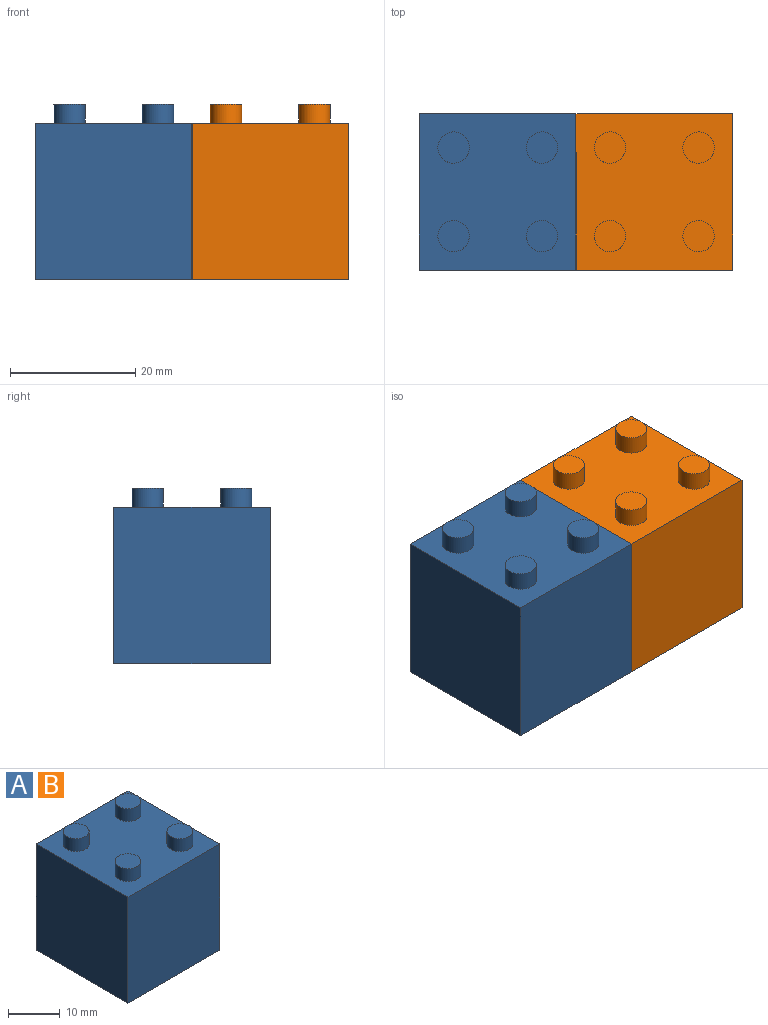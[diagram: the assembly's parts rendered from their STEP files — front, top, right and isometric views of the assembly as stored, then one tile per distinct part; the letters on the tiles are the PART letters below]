
ASSEMBLY  parts=2 mates=1
PART A: 23 faces, bbox 25x25x28 mm
  f0: plane 25x25mm, normal (0,0,-1), area 256.4mm2, adj f1,f2,f3,f4,f14,f15,f16,f17
  f1: plane 25x25mm, normal (1,0,0), area 625mm2, adj f0,f2,f4,f5
  f2: plane 25x25mm, normal (0,1,0), area 625mm2, adj f0,f1,f3,f5
  f3: plane 25x25mm, normal (-1,0,0), area 625mm2, adj f0,f2,f4,f5
  f4: plane 25x25mm, normal (0,-1,0), area 625mm2, adj f0,f1,f3,f5
  f5: plane 25x25mm, normal (0,0,1), area 546.5mm2, adj f1,f2,f3,f4,f6,f8,f10,f12
  f6: cylinder r=2.5mm len=5mm, axis (0,0,-1), area 47.1mm2, adj f5,f7
  f7: plane 5x5mm, normal (0,0,1), area 19.6mm2, adj f6
  f8: cylinder r=2.5mm len=5mm, axis (0,0,-1), area 47.1mm2, adj f5,f9
  f9: plane 5x5mm, normal (0,0,1), area 19.6mm2, adj f8
  f10: cylinder r=2.5mm len=5mm, axis (0,0,-1), area 47.1mm2, adj f5,f11
  f11: plane 5x5mm, normal (0,0,1), area 19.6mm2, adj f10
  f12: cylinder r=2.5mm len=5mm, axis (0,0,-1), area 47.1mm2, adj f5,f13
  f13: plane 5x5mm, normal (0,0,1), area 19.6mm2, adj f12
  f14: plane 22.1x19.2mm, normal (-1,0,0), area 424.3mm2, adj f0,f15,f17,f18
  f15: plane 22.1x19.2mm, normal (0,-1,0), area 424.3mm2, adj f0,f14,f16,f18
  f16: plane 22.1x19.2mm, normal (1,0,0), area 424.3mm2, adj f0,f15,f17,f18
  f17: plane 22.1x19.2mm, normal (0,1,0), area 424.3mm2, adj f0,f14,f16,f18
  f18: plane 19.2x19.2mm, normal (0,0,-1), area 194.3mm2, adj f14,f15,f16,f17,f20
  f19: cylinder r=6.5mm len=22mm, axis (0,0,1), area 898.5mm2, adj f21,f22
  f20: cylinder r=7.45mm len=22mm, axis (0,0,1), area 1029.8mm2, adj f18,f21
  f21: plane 14.9x14.9mm, normal (0,0,-1), area 41.6mm2, adj f19,f20
  f22: plane 13x13mm, normal (0,0,-1), area 132.7mm2, adj f19
PART B: same geometry as A
PLACE A t=(-3.71,20.87,-18.3)mm
PLACE B t=(21.29,20.87,-18.3)mm
MATE fastened A.f1 <-> B.f3  axis (1,0,0) through (-3.71,8.37,-5.8)mm
